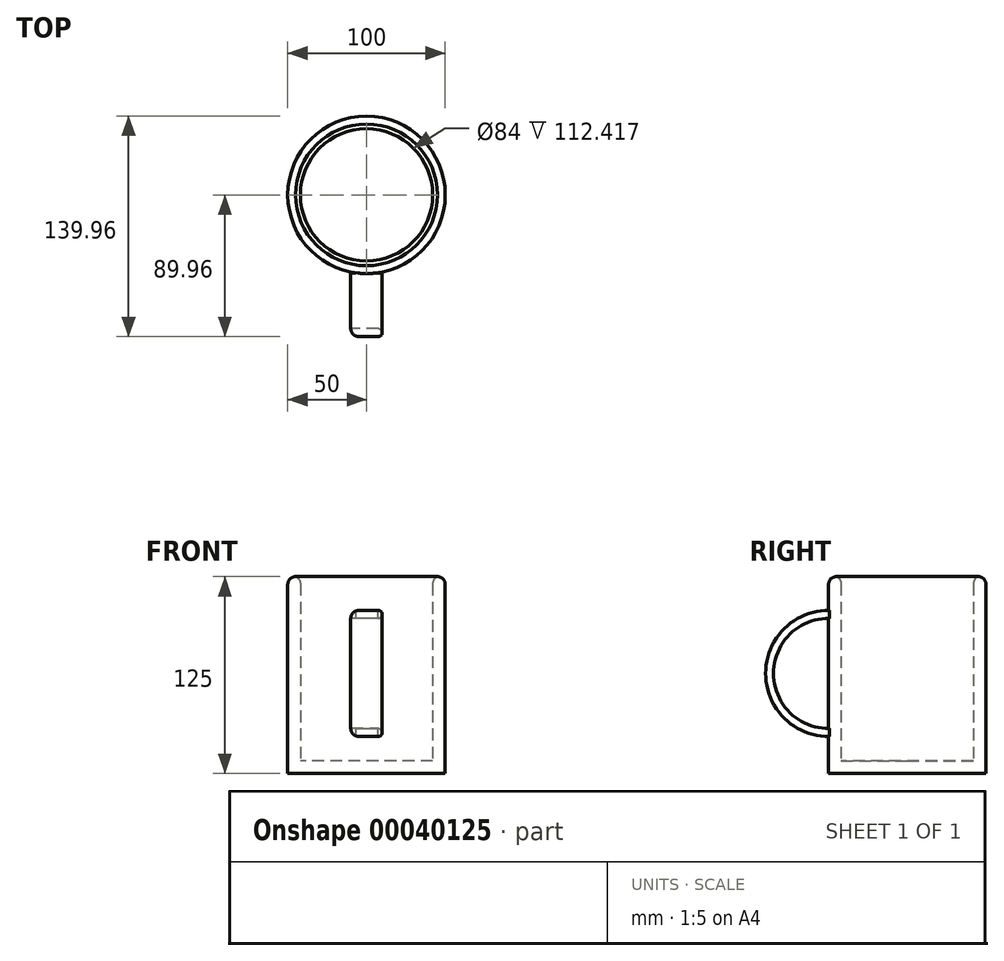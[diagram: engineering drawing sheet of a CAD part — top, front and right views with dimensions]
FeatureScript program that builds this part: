
annotation { "Feature Type Name" : "Feature", "Feature Type Description" : "" }
export const myFeature = defineFeature(function(context is Context, id is Id, definition is map)
    precondition{}
    {
        {
            var Q0;
            Q0=qCreatedBy(makeId("Top.planeOp"),FACE);
            var sketch = newSketch(context, id + "F0", { "sketchPlane" : qUnion([Q0])});
            skCircle(sketch, "E0", {"center": v(0, 0) * mm, "radius": 50 * mm});
            skSolve(sketch);
        }
        {
            var Q0;
            Q0=makeQuery(id+"F0.imprint","IMPRINT",FACE,{"disambiguationData":[TD([[makeQuery(id+"F0.imprint","IMPRINT",EDGE,{"derivedFrom":sQuery(id+"F0.wireOp",EDGE,"E0")}),1.0]])]});
            extrude(context, id + "F1", {"entities" : qUnion([Q0]), "depth" : 125 * mm});
        }
        {
            var Q0;
            Q0=makeQuery(id+"F1.opExtrude","CAP_FACE",FACE,{"disambiguationData":[OSD([sQuery(id+"F0.wireOp",EDGE,"E0")])],"isStart":false});
            shell(context, id + "F2", {"entities" : qUnion([Q0]), "thickness" : 8 * mm});
        }
        {
            var Q0;
            Q0=makeQuery(id+"F1.opExtrude","CAP_EDGE",EDGE,{"disambiguationData":[OSD([sQuery(id+"F0.wireOp",EDGE,"E0")])],"isStart":false});
            fillet(context, id + "F3", {"entities" : qUnion([Q0]), "radius" : 5 * mm, "tangentPropagation" : true, "allowEdgeOverflow" : false});
        }
        {
            var Q0;
            {var subQ0=sQuery(id+"F0.wireOp",EDGE,"E0");Q0=makeQuery(id+"F2.opShell","OFFSET_EDGE",EDGE,{"disambiguationData":[OSD([subQ0]),TDD([makeQuery(id+"F1.opExtrude","CAP_EDGE",EDGE,{"disambiguationData":[OSD([subQ0])],"isStart":false})])]});}
            fillet(context, id + "F4", {"entities" : qUnion([Q0]), "radius" : 5 * mm, "tangentPropagation" : true, "allowEdgeOverflow" : false});
        }
        {
            var Q0;
            Q0=qCreatedBy(makeId("Right.planeOp"),FACE);
            var sketch = newSketch(context, id + "F5", { "sketchPlane" : qUnion([Q0])});
            skArc(sketch, "E1", {"start": v(-49.5, 98.48) * mm, "mid": v(-84.96, 63.49) * mm, "end": v(-49.5, 28.49) * mm});
            skArc(sketch, "E2.0", {"start": v(-49.5, 103.48) * mm, "mid": v(-89.96, 63.49) * mm, "end": v(-49.5, 23.49) * mm});
            skLineSegment(sketch, "E3", {"start": v(-49.5, 103.48) * mm, "end": v(-49.5, 23.49) * mm});
            skSolve(sketch);
        }
        {
            var Q0;
            Q0=makeQuery(id+"F5.imprint","IMPRINT",FACE,{"disambiguationData":[TD([[makeQuery(id+"F5.imprint","IMPRINT",EDGE,{"derivedFrom":sQuery(id+"F5.wireOp",EDGE,"E1")}),-1.0]])]});
            extrude(context, id + "F6", {"entities" : qUnion([Q0]), "operationType" : NewBodyOperationType.ADD, "depth" : 10 * mm, "hasSecondDirection" : true, "secondDirectionOppositeDirection" : true, "secondDirectionDepth" : 10 * mm});
        }
        {
            var Q0;
            Q0=makeQuery(id+"F6.opExtrude","CAP_EDGE",EDGE,{"disambiguationData":[OSD([sQuery(id+"F5.wireOp",EDGE,"E2.0")])],"isStart":false});
            fillet(context, id + "F7", {"entities" : qUnion([Q0]), "radius" : 2.5 * mm, "tangentPropagation" : true, "allowEdgeOverflow" : false});
        }
        {
            var Q0;
            Q0=makeQuery(id+"F6.opExtrude","CAP_EDGE",EDGE,{"disambiguationData":[OSD([sQuery(id+"F5.wireOp",EDGE,"E1")])],"isStart":false});
            fillet(context, id + "F8", {"entities" : qUnion([Q0]), "radius" : 2.5 * mm, "tangentPropagation" : true, "allowEdgeOverflow" : false});
        }
        {
            var Q0;
            Q0=makeQuery(id+"F6.opExtrude","CAP_EDGE",EDGE,{"disambiguationData":[OSD([sQuery(id+"F5.wireOp",EDGE,"E2.0")])],"isStart":true});
            fillet(context, id + "F9", {"entities" : qUnion([Q0]), "radius" : 5 * mm, "tangentPropagation" : true, "allowEdgeOverflow" : false});
        }
    });
